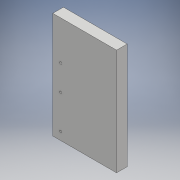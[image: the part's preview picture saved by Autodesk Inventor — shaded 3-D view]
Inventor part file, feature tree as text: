
AUTODESK INVENTOR PART (.ipt)
format: ipt  version: 2017 (Build 210142000, 142)  size: 113,152 bytes
history: native  units: mm
features: extrude x4, sketch x4
ambient origin geometry x8: Origin, YZ Plane, XZ Plane, XY Plane, X Axis, Y Axis, Z Axis, Center Point
bodies: Solid1 (feature_tree)
feature tree (8):
  extrude  "Extrusion1"  Depth=100.0mm
  extrude  "Extrusion2"  Depth=10.0mm
  extrude  "Extrusion3"  Depth=7.5mm
  extrude  "Extrusion4"  Depth=10.0mm
  sketch  "Sketch1"  dims[d0=60.0mm d1=100.0mm]
  sketch  "Sketch2"  dims[d2=10.0mm d3=0.0mm d4=2.0mm]
  sketch  "Sketch3"  dims[d5=39.375mm d6=7.5mm]
  sketch  "Sketch4"  dims[d7=10.0mm d8=0.0mm d9=2.0mm d10=24.0mm d11=0.0mm d12=10.0mm d13=0.0mm d14=2.0mm d15=7.5mm d16=7.5mm d17=10.0mm d18=0.0mm]
